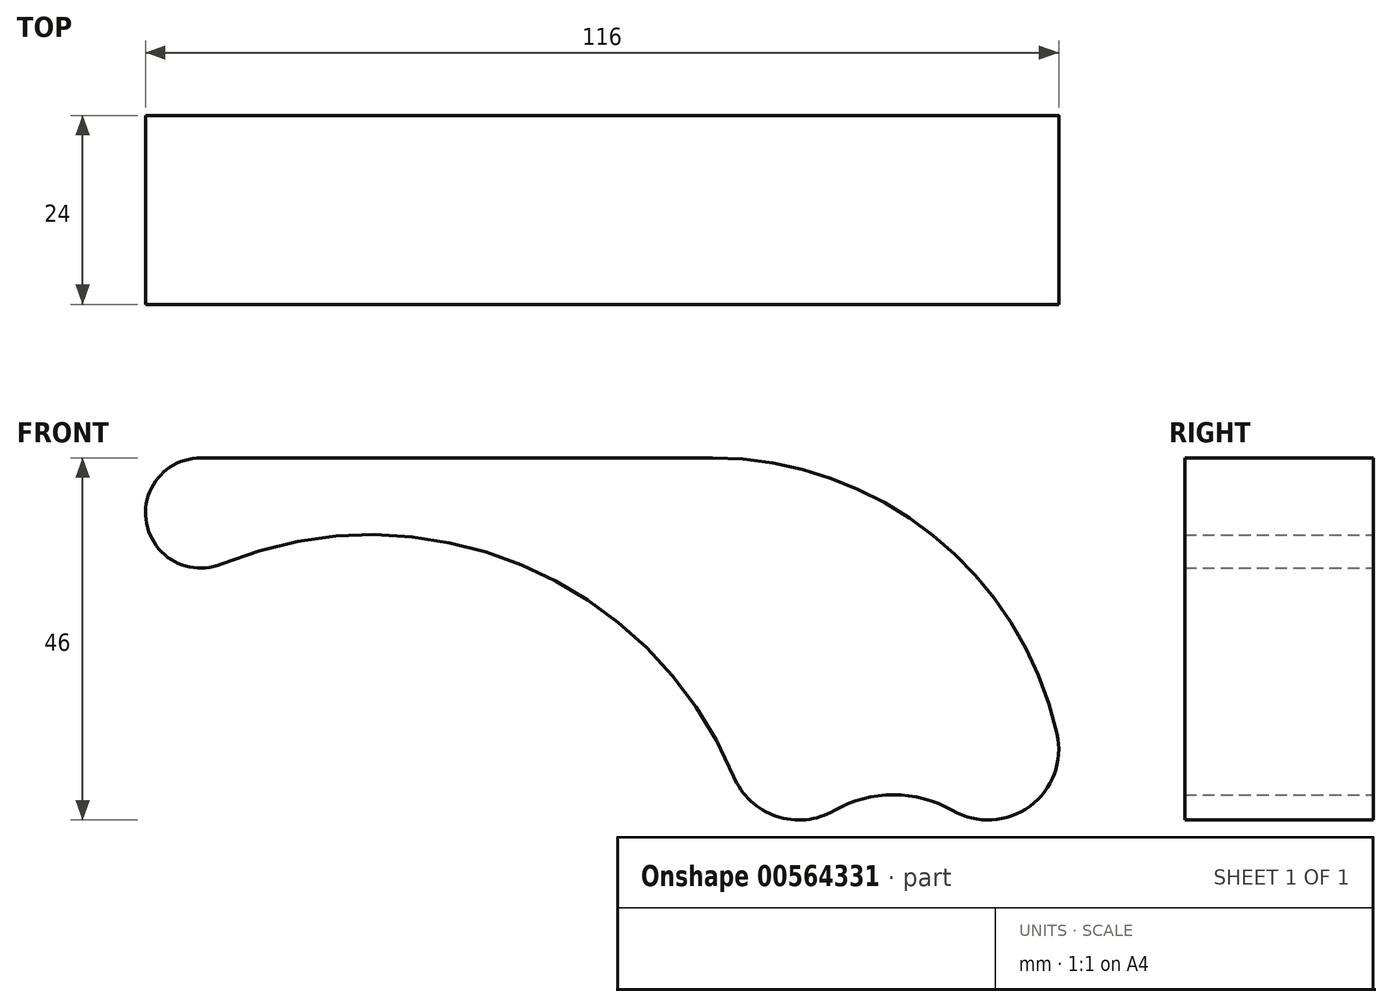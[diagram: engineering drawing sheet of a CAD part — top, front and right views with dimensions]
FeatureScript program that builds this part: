
annotation { "Feature Type Name" : "Feature", "Feature Type Description" : "" }
export const myFeature = defineFeature(function(context is Context, id is Id, definition is map)
    precondition{}
    {
        {
            var Q0;
            Q0=qCreatedBy(makeId("Front.planeOp"),FACE);
            var sketch = newSketch(context, id + "F0", { "sketchPlane" : qUnion([Q0])});
            skArc(sketch, "E0", {"start": v(-49.94, 28) * mm, "mid": v(-56.8, 19.65) * mm, "end": v(-47.29, 14.52) * mm});
            skArc(sketch, "E1", {"start": v(17.76, -12.47) * mm, "mid": v(23.19, -17.53) * mm, "end": v(30.56, -16.8) * mm});
            skArc(sketch, "E2", {"start": v(45.56, -16.8) * mm, "mid": v(55.4, -16.25) * mm, "end": v(58.84, -7.02) * mm});
            skPoint(sketch, "E3.first.point", {"position": v(-47.29, 14.52) * mm});
            skPoint(sketch, "E3.third.point", {"position": v(-83.7, -6.42) * mm});
            skArc(sketch, "E4", {"start": v(45.56, -16.8) * mm, "mid": v(38.06, -14.78) * mm, "end": v(30.56, -16.8) * mm});
            skArc(sketch, "E5", {"start": v(17.76, -12.47) * mm, "mid": v(-9.2, 14.42) * mm, "end": v(-47.29, 14.52) * mm});
            skLineSegment(sketch, "E6", {"start": v(-49.94, 28) * mm, "end": v(15.06, 28) * mm});
            skArc(sketch, "E7", {"start": v(58.84, -7.02) * mm, "mid": v(43.1, 18.17) * mm, "end": v(15.06, 28) * mm});
            skSolve(sketch);
        }
        {
            var Q0;
            Q0=makeQuery(id+"F0.imprint","IMPRINT",FACE,{"disambiguationData":[TD([[makeQuery(id+"F0.imprint","IMPRINT",EDGE,{"derivedFrom":sQuery(id+"F0.wireOp",EDGE,"E0")}),1.0]])]});
            extrude(context, id + "F1", {"entities" : qUnion([Q0]), "depth" : 24 * mm, "offsetDistance" : 25 * mm});
        }
    });
